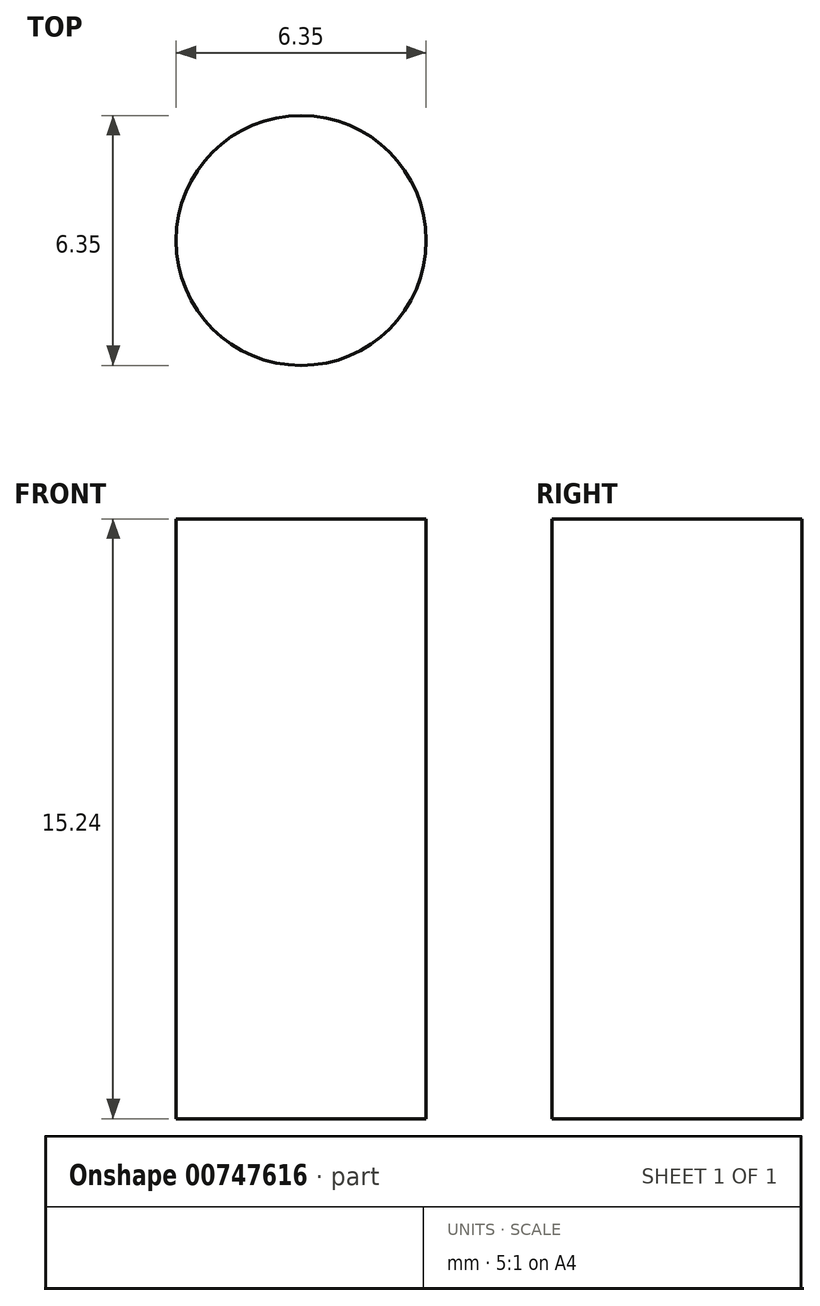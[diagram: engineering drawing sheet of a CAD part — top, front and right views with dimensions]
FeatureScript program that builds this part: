
annotation { "Feature Type Name" : "Feature", "Feature Type Description" : "" }
export const myFeature = defineFeature(function(context is Context, id is Id, definition is map)
    precondition{}
    {
        {
            var Q0;
            Q0=qCreatedBy(makeId("Front.planeOp"),FACE);
            var sketch = newSketch(context, id + "F0", { "sketchPlane" : qUnion([Q0])});
            skLineSegment(sketch, "E0.bottom", {"start": v(107.95, -7.62) * mm, "end": v(-107.95, -7.62) * mm});
            skLineSegment(sketch, "E0.top", {"start": v(107.95, 7.62) * mm, "end": v(-107.95, 7.62) * mm});
            skLineSegment(sketch, "E0.left", {"start": v(107.95, -7.62) * mm, "end": v(107.95, 7.62) * mm});
            skLineSegment(sketch, "E0.right", {"start": v(-107.95, -7.62) * mm, "end": v(-107.95, 7.62) * mm});
            skPoint(sketch, "E0.middle", {"position": v(0, 0) * mm});
            skSolve(sketch);
        }
        {
            var Q0;
            Q0=makeQuery(id+"F0.imprint","IMPRINT",FACE,{"disambiguationData":[TD([[makeQuery(id+"F0.imprint","IMPRINT",EDGE,{"derivedFrom":sQuery(id+"F0.wireOp",EDGE,"E0.bottom")}),-1.0]])]});
            extrude(context, id + "F1", {"entities" : qUnion([Q0]), "depth" : 12.7 * mm, "offsetDistance" : 25.4 * mm});
        }
        {
            var Q0;
            Q0=makeQuery(id+"F1.opExtrude","SWEPT_FACE",FACE,{"disambiguationData":[OSD([sQuery(id+"F0.wireOp",EDGE,"E0.top")])]});
            var sketch = newSketch(context, id + "F2", { "sketchPlane" : qUnion([Q0])});
            skCircle(sketch, "E1", {"center": v(-85.72, -8.9) * mm, "radius": 7.77 * mm});
            skCircle(sketch, "E2.1.0.0", {"center": v(-66.67, -8.9) * mm, "radius": 7.77 * mm});
            skCircle(sketch, "E2.2.0.0", {"center": v(-47.62, -8.89) * mm, "radius": 7.77 * mm});
            skCircle(sketch, "E2.3.0.0", {"center": v(-28.57, -8.89) * mm, "radius": 7.77 * mm});
            skCircle(sketch, "E2.4.0.0", {"center": v(-9.52, -8.89) * mm, "radius": 7.77 * mm});
            skCircle(sketch, "E2.5.0.0", {"center": v(9.53, -8.89) * mm, "radius": 7.77 * mm});
            skCircle(sketch, "E2.6.0.0", {"center": v(28.58, -8.89) * mm, "radius": 7.77 * mm});
            skCircle(sketch, "E2.7.0.0", {"center": v(47.63, -8.89) * mm, "radius": 7.77 * mm});
            skCircle(sketch, "E2.8.0.0", {"center": v(66.68, -8.89) * mm, "radius": 7.77 * mm});
            skCircle(sketch, "E2.9.0.0", {"center": v(85.73, -8.89) * mm, "radius": 7.77 * mm});
            skLineSegment(sketch, "E2.direction1", {"start": v(-85.72, -8.9) * mm, "end": v(-66.67, -8.89) * mm, "construction": true});
            skSolve(sketch);
        }
        {
            var Q0;
            Q0 = qSketchRegion(id + "F2", true);
            extrude(context, id + "F3", {"entities" : qUnion([Q0]), "operationType" : NewBodyOperationType.REMOVE, "oppositeDirection" : true, "depth" : 15.24 * mm, "offsetDistance" : 25.4 * mm});
        }
        {
            var Q0;
            Q0=makeQuery(id+"F1.opExtrude","SWEPT_FACE",FACE,{"disambiguationData":[OSD([sQuery(id+"F0.wireOp",EDGE,"E0.top")])]});
            var sketch = newSketch(context, id + "F4", { "sketchPlane" : qUnion([Q0])});
            skCircle(sketch, "E3", {"center": v(-100.6, -6.17) * mm, "radius": 3.18 * mm});
            skCircle(sketch, "E4.MirrorC", {"center": v(100.6, -6.17) * mm, "radius": 3.18 * mm});
            skSolve(sketch);
        }
        {
            var Q0;
            Q0=makeQuery(id+"F4.imprint","IMPRINT",FACE,{"disambiguationData":[TD([[makeQuery(id+"F4.imprint","IMPRINT",EDGE,{"derivedFrom":sQuery(id+"F4.wireOp",EDGE,"E3")}),1.0]])]});
            var Q1;
            Q1=makeQuery(id+"F4.imprint","IMPRINT",FACE,{"disambiguationData":[TD([[makeQuery(id+"F4.imprint","IMPRINT",EDGE,{"derivedFrom":sQuery(id+"F4.wireOp",EDGE,"E4.MirrorC")}),-1.0]])]});
            extrude(context, id + "F5", {"entities" : qUnion([Q0, Q1]), "operationType" : NewBodyOperationType.REMOVE, "endBound" : BoundingType.THROUGH_ALL, "oppositeDirection" : true, "depth" : 25.4 * mm, "offsetDistance" : 25.4 * mm});
        }
    });
